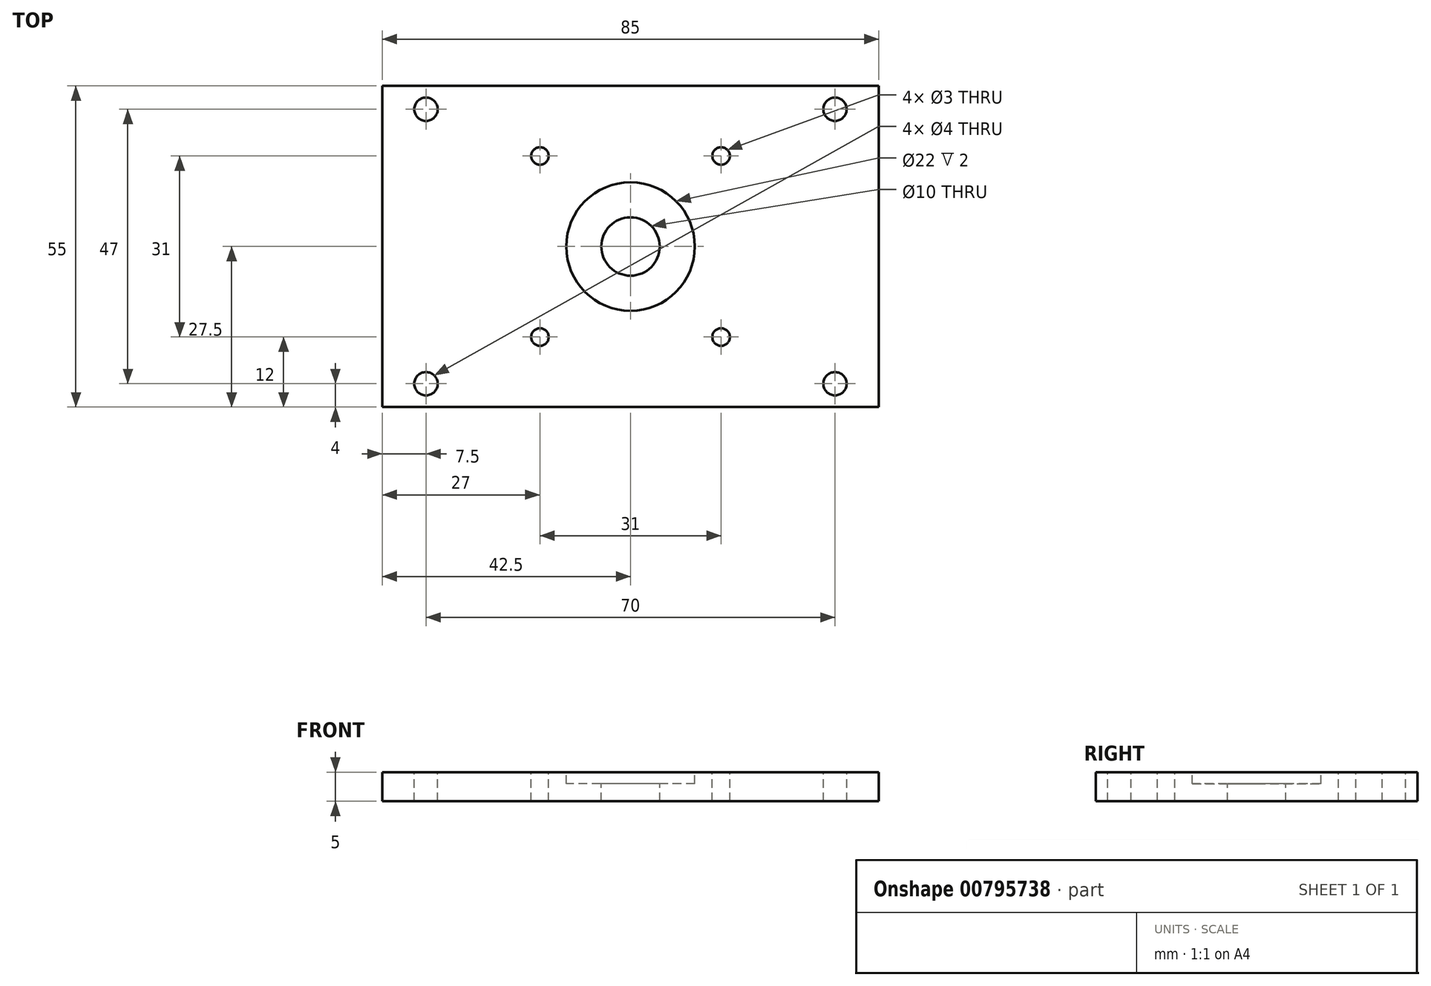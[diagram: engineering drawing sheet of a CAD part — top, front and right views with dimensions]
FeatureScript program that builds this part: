
annotation { "Feature Type Name" : "Feature", "Feature Type Description" : "" }
export const myFeature = defineFeature(function(context is Context, id is Id, definition is map)
    precondition{}
    {
        {
            var Q0;
            Q0=qCreatedBy(makeId("Top.planeOp"),FACE);
            var sketch = newSketch(context, id + "F0", { "sketchPlane" : qUnion([Q0])});
            skLineSegment(sketch, "E0.bottom", {"start": v(-42.5, -27.5) * mm, "end": v(42.5, -27.5) * mm});
            skLineSegment(sketch, "E0.top", {"start": v(-42.5, 27.5) * mm, "end": v(42.5, 27.5) * mm});
            skLineSegment(sketch, "E0.left", {"start": v(-42.5, -27.5) * mm, "end": v(-42.5, 27.5) * mm});
            skLineSegment(sketch, "E0.right", {"start": v(42.5, -27.5) * mm, "end": v(42.5, 27.5) * mm});
            skPoint(sketch, "E0.middle", {"position": v(0, 0) * mm});
            skSolve(sketch);
        }
        {
            var Q0;
            Q0=makeQuery(id+"F0.imprint","IMPRINT",FACE,{"disambiguationData":[TD([[makeQuery(id+"F0.imprint","IMPRINT",EDGE,{"derivedFrom":sQuery(id+"F0.wireOp",EDGE,"E0.bottom")}),1.0]])]});
            extrude(context, id + "F1", {"entities" : qUnion([Q0]), "depth" : 5 * mm, "offsetDistance" : 25 * mm});
        }
        {
            var Q0;
            Q0=makeQuery(id+"F1.opExtrude","CAP_FACE",FACE,{"disambiguationData":[OSD([sQuery(id+"F0.wireOp",EDGE,"E0.bottom"),sQuery(id+"F0.wireOp",EDGE,"E0.top"),sQuery(id+"F0.wireOp",EDGE,"E0.left"),sQuery(id+"F0.wireOp",EDGE,"E0.right")])],"isStart":false});
            var sketch = newSketch(context, id + "F2", { "sketchPlane" : qUnion([Q0])});
            skCircle(sketch, "E1", {"center": v(0, 0) * mm, "radius": 11 * mm});
            skSolve(sketch);
        }
        {
            var Q0;
            Q0 = qSketchRegion(id + "F2", true);
            extrude(context, id + "F3", {"entities" : qUnion([Q0]), "operationType" : NewBodyOperationType.REMOVE, "oppositeDirection" : true, "depth" : 2 * mm, "offsetDistance" : 25 * mm});
        }
        {
            var Q0;
            Q0=makeQuery(id+"F3.boolean.opBoolean","COPY",FACE,{"derivedFrom":makeQuery(id+"F3.opExtrude","CAP_FACE",FACE,{"disambiguationData":[OSD([sQuery(id+"F2.wireOp",EDGE,"E1")])],"isStart":false})});
            var sketch = newSketch(context, id + "F4", { "sketchPlane" : qUnion([Q0])});
            skCircle(sketch, "E2", {"center": v(0, 0) * mm, "radius": 5 * mm});
            skSolve(sketch);
        }
        {
            var Q0;
            Q0 = qSketchRegion(id + "F4", true);
            extrude(context, id + "F5", {"entities" : qUnion([Q0]), "operationType" : NewBodyOperationType.REMOVE, "endBound" : BoundingType.THROUGH_ALL, "oppositeDirection" : true, "depth" : 25 * mm, "offsetDistance" : 25 * mm});
        }
        {
            var Q0;
            Q0=makeQuery(id+"F1.opExtrude","CAP_FACE",FACE,{"disambiguationData":[OSD([sQuery(id+"F0.wireOp",EDGE,"E0.bottom"),sQuery(id+"F0.wireOp",EDGE,"E0.top"),sQuery(id+"F0.wireOp",EDGE,"E0.left"),sQuery(id+"F0.wireOp",EDGE,"E0.right")])],"isStart":false});
            var sketch = newSketch(context, id + "F6", { "sketchPlane" : qUnion([Q0])});
            skLineSegment(sketch, "E3", {"start": v(0, 0) * mm, "end": v(0, 15.5) * mm, "construction": true});
            skLineSegment(sketch, "E4", {"start": v(0, 15.5) * mm, "end": v(-15.5, 15.5) * mm, "construction": true});
            skLineSegment(sketch, "E5", {"start": v(-15.5, 15.5) * mm, "end": v(-15.5, -15.5) * mm, "construction": true});
            skLineSegment(sketch, "E6", {"start": v(-15.5, -15.5) * mm, "end": v(15.5, -15.5) * mm, "construction": true});
            skLineSegment(sketch, "E7", {"start": v(15.5, -15.5) * mm, "end": v(15.5, 15.5) * mm, "construction": true});
            skCircle(sketch, "E8", {"center": v(-15.5, 15.5) * mm, "radius": 1.5 * mm});
            skCircle(sketch, "E9", {"center": v(-15.5, -15.5) * mm, "radius": 1.5 * mm});
            skCircle(sketch, "E10", {"center": v(15.5, -15.5) * mm, "radius": 1.5 * mm});
            skCircle(sketch, "E11", {"center": v(15.5, 15.5) * mm, "radius": 1.5 * mm});
            skSolve(sketch);
        }
        {
            var Q0;
            Q0=makeQuery(id+"F6.imprint","IMPRINT",FACE,{"disambiguationData":[TD([[makeQuery(id+"F6.imprint","IMPRINT",EDGE,{"derivedFrom":sQuery(id+"F6.wireOp",EDGE,"E8")}),1.0]])]});
            var Q1;
            Q1=makeQuery(id+"F6.imprint","IMPRINT",FACE,{"disambiguationData":[TD([[makeQuery(id+"F6.imprint","IMPRINT",EDGE,{"derivedFrom":sQuery(id+"F6.wireOp",EDGE,"E11")}),1.0]])]});
            var Q2;
            Q2=makeQuery(id+"F6.imprint","IMPRINT",FACE,{"disambiguationData":[TD([[makeQuery(id+"F6.imprint","IMPRINT",EDGE,{"derivedFrom":sQuery(id+"F6.wireOp",EDGE,"E10")}),1.0]])]});
            var Q3;
            Q3=makeQuery(id+"F6.imprint","IMPRINT",FACE,{"disambiguationData":[TD([[makeQuery(id+"F6.imprint","IMPRINT",EDGE,{"derivedFrom":sQuery(id+"F6.wireOp",EDGE,"E9")}),1.0]])]});
            extrude(context, id + "F7", {"entities" : qUnion([Q0, Q1, Q2, Q3]), "operationType" : NewBodyOperationType.REMOVE, "endBound" : BoundingType.THROUGH_ALL, "oppositeDirection" : true, "depth" : 25 * mm, "offsetDistance" : 25 * mm});
        }
        {
            var Q0;
            Q0=makeQuery(id+"F1.opExtrude","CAP_FACE",FACE,{"disambiguationData":[OSD([sQuery(id+"F0.wireOp",EDGE,"E0.bottom"),sQuery(id+"F0.wireOp",EDGE,"E0.top"),sQuery(id+"F0.wireOp",EDGE,"E0.left"),sQuery(id+"F0.wireOp",EDGE,"E0.right")])],"isStart":false});
            var sketch = newSketch(context, id + "F8", { "sketchPlane" : qUnion([Q0])});
            skLineSegment(sketch, "E12", {"start": v(42.5, 0) * mm, "end": v(35, 0) * mm, "construction": true});
            skLineSegment(sketch, "E13", {"start": v(35, 0) * mm, "end": v(35, 23.5) * mm, "construction": true});
            skLineSegment(sketch, "E14", {"start": v(35, 0) * mm, "end": v(35, -23.5) * mm, "construction": true});
            skCircle(sketch, "E15", {"center": v(35, -23.5) * mm, "radius": 2 * mm});
            skCircle(sketch, "E16", {"center": v(35, 23.5) * mm, "radius": 2 * mm});
            skLineSegment(sketch, "E17", {"start": v(-42.5, 0) * mm, "end": v(-35, 0) * mm, "construction": true});
            skLineSegment(sketch, "E18", {"start": v(-35, 0) * mm, "end": v(-35, -23.5) * mm, "construction": true});
            skLineSegment(sketch, "E19", {"start": v(-35, 0) * mm, "end": v(-35, 23.5) * mm, "construction": true});
            skCircle(sketch, "E20", {"center": v(-35, -23.5) * mm, "radius": 2 * mm});
            skCircle(sketch, "E21", {"center": v(-35, 23.5) * mm, "radius": 2 * mm});
            skSolve(sketch);
        }
        {
            var Q0;
            Q0=makeQuery(id+"F8.imprint","IMPRINT",FACE,{"disambiguationData":[TD([[makeQuery(id+"F8.imprint","IMPRINT",EDGE,{"derivedFrom":sQuery(id+"F8.wireOp",EDGE,"E20")}),1.0]])]});
            var Q1;
            Q1=makeQuery(id+"F8.imprint","IMPRINT",FACE,{"disambiguationData":[TD([[makeQuery(id+"F8.imprint","IMPRINT",EDGE,{"derivedFrom":sQuery(id+"F8.wireOp",EDGE,"E21")}),1.0]])]});
            var Q2;
            Q2=makeQuery(id+"F8.imprint","IMPRINT",FACE,{"disambiguationData":[TD([[makeQuery(id+"F8.imprint","IMPRINT",EDGE,{"derivedFrom":sQuery(id+"F8.wireOp",EDGE,"E16")}),1.0]])]});
            var Q3;
            Q3=makeQuery(id+"F8.imprint","IMPRINT",FACE,{"disambiguationData":[TD([[makeQuery(id+"F8.imprint","IMPRINT",EDGE,{"derivedFrom":sQuery(id+"F8.wireOp",EDGE,"E15")}),1.0]])]});
            extrude(context, id + "F9", {"entities" : qUnion([Q0, Q1, Q2, Q3]), "operationType" : NewBodyOperationType.REMOVE, "endBound" : BoundingType.THROUGH_ALL, "oppositeDirection" : true, "depth" : 25 * mm, "offsetDistance" : 25 * mm});
        }
    });
